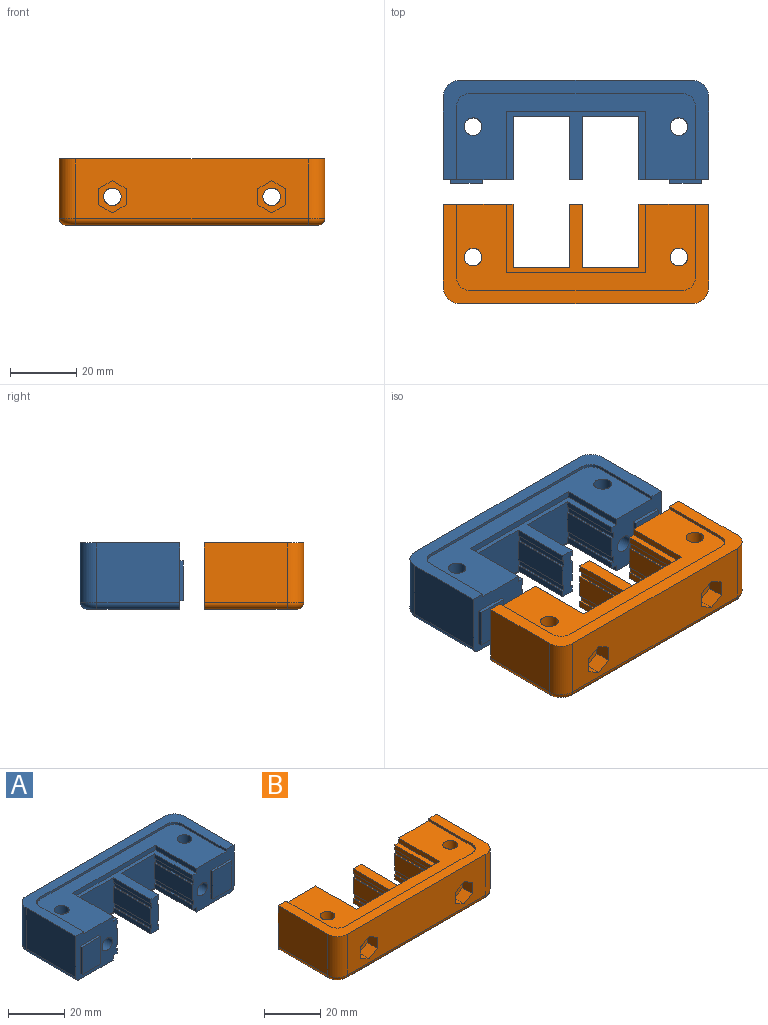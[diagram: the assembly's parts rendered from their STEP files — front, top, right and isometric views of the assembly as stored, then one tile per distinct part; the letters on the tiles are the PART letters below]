
ASSEMBLY  parts=2 mates=2
PART A: 89 faces, bbox 80.8x31.4x19.9 mm
  f0: plane 10.4x10.4mm, normal (0,0,-1), area 62.9mm2, adj f3,f9
  f1: plane 10.4x10.4mm, normal (0,0,-1), area 62.9mm2, adj f4,f10
  f2: cylinder r=2mm len=70mm, axis (1,0,0), area 219.9mm2, adj f5,f15,f16,f39
  f3: cylinder r=5.2mm len=10.4mm, axis (0,0,-1), area 163.4mm2, adj f0,f39
  f4: cylinder r=5.2mm len=10.4mm, axis (0,0,-1), area 163.4mm2, adj f1,f39
  f5: plane 70x17.9mm, normal (0,1,0), area 1083.1mm2, adj f2,f6,f7,f38,f70,f73
  f6: cylinder r=5mm len=17.9mm, axis (0,0,-1), area 140.6mm2, adj f5,f15,f37,f38
  f7: cylinder r=5mm len=17.9mm, axis (0,0,-1), area 140.6mm2, adj f5,f16,f35,f38
  f8: plane 64x0.9mm, normal (0,-1,0), area 57.6mm2, adj f11,f12,f33,f38
  f9: cylinder r=2.65mm len=14mm, axis (0,0,-1), area 233.1mm2, adj f0,f33
  f10: cylinder r=2.65mm len=14mm, axis (0,0,-1), area 233.1mm2, adj f1,f33
  f11: cylinder r=4mm len=4mm, axis (0,0,1), area 5.7mm2, adj f8,f32,f33,f38
  f12: cylinder r=4mm len=4mm, axis (0,0,1), area 5.7mm2, adj f8,f28,f33,f38
  f13: plane 41.9x2mm, normal (0,-1,0), area 83.8mm2, adj f25,f26,f27,f39
  f14: plane 41.9x2mm, normal (0,-1,0), area 83.8mm2, adj f29,f30,f31,f33
  f15: torus R=3mm, axis (0,0,-1), area 21.1mm2, adj f2,f6,f36,f39
  f16: torus R=3mm, axis (0,0,-1), area 21.1mm2, adj f2,f7,f34,f39
  f17: plane 18x15mm, normal (0,-1,0), area 258.4mm2, adj f25,f31,f40,f41,f42,f43,f44,f45
  f18: plane 18x15mm, normal (0,-1,0), area 258.4mm2, adj f19,f20,f21,f22,f23,f24,f25,f31
  f19: plane 19x2mm, normal (-1,0,0), area 38mm2, adj f18,f20,f21,f76
  f20: plane 19x0.53mm, normal (0,0,1), area 10mm2, adj f18,f19,f69,f76
  f21: plane 19x0.53mm, normal (0,0,-1), area 10mm2, adj f18,f19,f49,f76
  f22: plane 19x0.53mm, normal (0,0,-1), area 10mm2, adj f18,f24,f48,f77
  f23: plane 19x0.53mm, normal (0,0,1), area 10mm2, adj f18,f24,f64,f77
  f24: plane 19x2mm, normal (1,0,0), area 38mm2, adj f18,f22,f23,f77
  f25: plane 41.9x20.5mm, normal (0,0,-1), area 214.8mm2, adj f13,f17,f18,f26,f27,f54,f59,f63
  f26: plane 20.5x2mm, normal (1,0,0), area 41mm2, adj f13,f25,f39,f78
  f27: plane 20.5x2mm, normal (-1,0,0), area 41mm2, adj f13,f25,f39,f76
  f28: plane 22x0.9mm, normal (-1,0,0), area 19.8mm2, adj f12,f33,f38,f76
  f29: plane 20.5x2mm, normal (-1,0,0), area 41mm2, adj f14,f31,f33,f76
  f30: plane 20.5x2mm, normal (1,0,0), area 41mm2, adj f14,f31,f33,f78
  f31: plane 41.9x20.5mm, normal (0,0,1), area 214.9mm2, adj f14,f17,f18,f29,f30,f43,f47,f48
  f32: plane 22x0.9mm, normal (1,0,0), area 19.8mm2, adj f11,f33,f38,f78
  f33: plane 72x26mm, normal (0,0,1), area 962.1mm2, adj f8,f9,f10,f11,f12,f14,f28,f29
  f34: cylinder r=2mm len=25mm, axis (0,1,0), area 78.5mm2, adj f16,f35,f39,f78
  f35: plane 25x17.9mm, normal (-1,0,0), area 447.5mm2, adj f7,f34,f38,f78
  f36: cylinder r=2mm len=25mm, axis (0,-1,0), area 78.5mm2, adj f15,f37,f39,f76
  f37: plane 25x17.9mm, normal (1,0,0), area 447.5mm2, adj f6,f36,f38,f76
  f38: plane 80x30mm, normal (0,0,1), area 524.1mm2, adj f5,f6,f7,f8,f11,f12,f28,f32
  f39: plane 76x28mm, normal (0,0,-1), area 1095.3mm2, adj f2,f3,f4,f13,f15,f16,f26,f27
  f40: plane 19x0.53mm, normal (0,0,-1), area 10mm2, adj f17,f42,f43,f77
  f41: plane 19x0.53mm, normal (0,0,1), area 10mm2, adj f17,f42,f53,f77
  f42: plane 19x2mm, normal (-1,0,0), area 38mm2, adj f17,f40,f41,f77
  f43: plane 19x2mm, normal (-1,0,0), area 38mm2, adj f17,f31,f40,f77
  f44: plane 19x2mm, normal (1,0,0), area 38mm2, adj f17,f45,f46,f78
  f45: plane 19x0.53mm, normal (0,0,1), area 10mm2, adj f17,f44,f58,f78
  f46: plane 19x0.53mm, normal (0,0,-1), area 10mm2, adj f17,f44,f47,f78
  f47: plane 19x2mm, normal (1,0,0), area 38mm2, adj f17,f31,f46,f78
  f48: plane 19x2mm, normal (1,0,0), area 38mm2, adj f18,f22,f31,f77
  f49: plane 19x2mm, normal (-1,0,0), area 38mm2, adj f18,f21,f31,f76
  f50: plane 19x0.53mm, normal (0,0,-1), area 10mm2, adj f17,f52,f53,f77
  f51: plane 19x0.53mm, normal (0,0,1), area 10mm2, adj f17,f52,f54,f77
  f52: plane 19x2mm, normal (-1,0,0), area 38mm2, adj f17,f50,f51,f77
  f53: plane 19x7mm, normal (-1,0,0), area 133mm2, adj f17,f41,f50,f77
  f54: plane 19x2mm, normal (-1,0,0), area 38mm2, adj f17,f25,f51,f77
  f55: plane 19x2mm, normal (1,0,0), area 38mm2, adj f17,f56,f57,f78
  f56: plane 19x0.53mm, normal (0,0,1), area 10mm2, adj f17,f55,f59,f78
  f57: plane 19x0.53mm, normal (0,0,-1), area 10mm2, adj f17,f55,f58,f78
  f58: plane 19x7mm, normal (1,0,0), area 133mm2, adj f17,f45,f57,f78
  f59: plane 19x2mm, normal (1,0,0), area 38mm2, adj f17,f25,f56,f78
  f60: plane 19x0.53mm, normal (0,0,-1), area 10mm2, adj f18,f62,f64,f77
  f61: plane 19x0.53mm, normal (0,0,1), area 10mm2, adj f18,f62,f63,f77
  f62: plane 19x2mm, normal (1,0,0), area 38mm2, adj f18,f60,f61,f77
  f63: plane 19x2mm, normal (1,0,0), area 38mm2, adj f18,f25,f61,f77
  f64: plane 19x7mm, normal (1,0,0), area 133mm2, adj f18,f23,f60,f77
  f65: plane 19x2mm, normal (-1,0,0), area 38mm2, adj f18,f66,f67,f76
  f66: plane 19x0.53mm, normal (0,0,1), area 10mm2, adj f18,f65,f68,f76
  f67: plane 19x0.53mm, normal (0,0,-1), area 10mm2, adj f18,f65,f69,f76
  f68: plane 19x2mm, normal (-1,0,0), area 38mm2, adj f18,f25,f66,f76
  f69: plane 19x7mm, normal (-1,0,0), area 133mm2, adj f18,f20,f67,f76
  f70: cylinder r=5.2mm len=10.4mm, axis (0,1,0), area 163.4mm2, adj f5,f71
  f71: plane 10.4x10.4mm, normal (0,1,0), area 62.9mm2, adj f70,f72
  f72: cylinder r=2.65mm len=25mm, axis (0,1,0), area 416.3mm2, adj f71,f78
  f73: cylinder r=5.2mm len=10.4mm, axis (0,1,0), area 163.4mm2, adj f5,f74
  f74: plane 10.4x10.4mm, normal (0,1,0), area 62.9mm2, adj f73,f75
  f75: cylinder r=2.65mm len=25mm, axis (0,1,0), area 416.3mm2, adj f74,f76
  f76: plane 21.05x19.9mm, normal (0,-1,0), area 256.5mm2, adj f19,f20,f21,f25,f27,f28,f29,f31
  f77: plane 15x4mm, normal (0,-1,0), area 55.8mm2, adj f22,f23,f24,f25,f31,f40,f41,f42
  f78: plane 21.05x19.9mm, normal (0,-1,0), area 256.5mm2, adj f25,f26,f30,f31,f32,f33,f34,f35
  f79: plane 9.5x1mm, normal (0,0,-1), area 9.5mm2, adj f76,f80,f82,f83
  f80: plane 12x1mm, normal (1,0,0), area 12mm2, adj f76,f79,f81,f83
  f81: plane 9.5x1mm, normal (0,0,1), area 9.5mm2, adj f76,f80,f82,f83
  f82: plane 12x1mm, normal (-1,0,0), area 12mm2, adj f76,f79,f81,f83
  f83: plane 12x9.5mm, normal (0,-1,0), area 114mm2, adj f79,f80,f81,f82
  f84: plane 9.5x1mm, normal (0,0,1), area 9.5mm2, adj f78,f85,f87,f88
  f85: plane 12x1mm, normal (-1,0,0), area 12mm2, adj f78,f84,f86,f88
  f86: plane 9.5x1mm, normal (0,0,-1), area 9.5mm2, adj f78,f85,f87,f88
  f87: plane 12x1mm, normal (1,0,0), area 12mm2, adj f78,f84,f86,f88
  f88: plane 12x9.5mm, normal (0,-1,0), area 114mm2, adj f84,f85,f86,f87
PART B: 99 faces, bbox 80.8x30.4x19.9 mm
  f0: plane 21.05x19.9mm, normal (0,1,0), area 247.8mm2, adj f2,f3,f10,f16,f17,f20,f22,f45
  f1: plane 21.05x19.9mm, normal (0,1,0), area 247.8mm2, adj f6,f7,f12,f16,f17,f21,f26,f45
  f2: plane 19x7mm, normal (-1,0,0), area 133mm2, adj f0,f15,f82,f86
  f3: plane 19x2mm, normal (-1,0,0), area 38mm2, adj f0,f15,f54,f83
  f4: plane 19x7mm, normal (1,0,0), area 133mm2, adj f15,f78,f80,f88
  f5: plane 19x2mm, normal (1,0,0), area 38mm2, adj f15,f54,f77,f88
  f6: plane 19x2mm, normal (1,0,0), area 38mm2, adj f1,f14,f54,f74
  f7: plane 19x7mm, normal (1,0,0), area 133mm2, adj f1,f14,f71,f73
  f8: plane 19x2mm, normal (-1,0,0), area 38mm2, adj f14,f54,f68,f88
  f9: plane 19x7mm, normal (-1,0,0), area 133mm2, adj f14,f65,f69,f88
  f10: plane 19x2mm, normal (-1,0,0), area 38mm2, adj f0,f15,f55,f85
  f11: plane 19x2mm, normal (1,0,0), area 38mm2, adj f15,f55,f81,f88
  f12: plane 19x2mm, normal (1,0,0), area 38mm2, adj f1,f14,f55,f70
  f13: plane 19x2mm, normal (-1,0,0), area 38mm2, adj f14,f55,f66,f88
  f14: plane 18x15mm, normal (0,1,0), area 258.4mm2, adj f6,f7,f8,f9,f12,f13,f54,f55
  f15: plane 18x15mm, normal (0,1,0), area 258.4mm2, adj f2,f3,f4,f5,f10,f11,f54,f55
  f16: plane 76x28mm, normal (0,0,-1), area 1095.3mm2, adj f0,f1,f28,f30,f51,f52,f53,f59
  f17: plane 80x30mm, normal (0,0,1), area 524.1mm2, adj f0,f1,f22,f23,f24,f25,f26,f46
  f18: cylinder r=2.65mm len=14mm, axis (0,0,-1), area 233.1mm2, adj f27,f45
  f19: cylinder r=2.65mm len=14mm, axis (0,0,-1), area 233.1mm2, adj f29,f45
  f20: cylinder r=2.65mm len=25mm, axis (0,1,0), area 416.3mm2, adj f0,f44
  f21: cylinder r=2.65mm len=25mm, axis (0,1,0), area 416.3mm2, adj f1,f37
  f22: plane 25x17.9mm, normal (1,0,0), area 447.5mm2, adj f0,f17,f23,f59
  f23: cylinder r=5mm len=17.9mm, axis (0,0,-1), area 140.6mm2, adj f17,f22,f24,f60
  f24: plane 70x17.9mm, normal (0,-1,0), area 1130.8mm2, adj f17,f23,f25,f31,f32,f33,f34,f35
  f25: cylinder r=5mm len=17.9mm, axis (0,0,-1), area 140.6mm2, adj f17,f24,f26,f62
  f26: plane 25x17.9mm, normal (-1,0,0), area 447.5mm2, adj f1,f17,f25,f63
  f27: plane 10.4x10.4mm, normal (0,0,-1), area 62.9mm2, adj f18,f28
  f28: cylinder r=5.2mm len=10.4mm, axis (0,0,-1), area 163.4mm2, adj f16,f27
  f29: plane 10.4x10.4mm, normal (0,0,-1), area 62.9mm2, adj f19,f30
  f30: cylinder r=5.2mm len=10.4mm, axis (0,0,-1), area 163.4mm2, adj f16,f29
  f31: plane 5x4.2mm, normal (0.5,0,-0.87), area 24.2mm2, adj f24,f32,f36,f37
  f32: plane 5x4.85mm, normal (1,0,0), area 24.2mm2, adj f24,f31,f33,f37
  f33: plane 5x4.2mm, normal (0.5,0,0.87), area 24.2mm2, adj f24,f32,f34,f37
  f34: plane 5x4.2mm, normal (-0.5,0,0.87), area 24.2mm2, adj f24,f33,f35,f37
  f35: plane 5x4.85mm, normal (-1,0,0), area 24.2mm2, adj f24,f34,f36,f37
  f36: plane 5x4.2mm, normal (-0.5,0,-0.87), area 24.2mm2, adj f24,f31,f35,f37
  f37: plane 9.7x8.4mm, normal (0,-1,0), area 39mm2, adj f21,f31,f32,f33,f34,f35,f36
  f38: plane 5x4.2mm, normal (0.5,0,-0.87), area 24.2mm2, adj f24,f39,f43,f44
  f39: plane 5x4.85mm, normal (1,0,0), area 24.2mm2, adj f24,f38,f40,f44
  f40: plane 5x4.2mm, normal (0.5,0,0.87), area 24.2mm2, adj f24,f39,f41,f44
  f41: plane 5x4.2mm, normal (-0.5,0,0.87), area 24.2mm2, adj f24,f40,f42,f44
  f42: plane 5x4.85mm, normal (-1,0,0), area 24.2mm2, adj f24,f41,f43,f44
  f43: plane 5x4.2mm, normal (-0.5,0,-0.87), area 24.2mm2, adj f24,f38,f42,f44
  f44: plane 9.7x8.4mm, normal (0,-1,0), area 39mm2, adj f20,f38,f39,f40,f41,f42,f43
  f45: plane 72x26mm, normal (0,0,1), area 962.1mm2, adj f0,f1,f18,f19,f46,f47,f48,f49
  f46: plane 22x0.9mm, normal (1,0,0), area 19.8mm2, adj f1,f17,f45,f47
  f47: cylinder r=4mm len=4mm, axis (0,0,1), area 5.7mm2, adj f17,f45,f46,f48
  f48: plane 64x0.9mm, normal (0,1,0), area 57.6mm2, adj f17,f45,f47,f49
  f49: cylinder r=4mm len=4mm, axis (0,0,1), area 5.7mm2, adj f17,f45,f48,f50
  f50: plane 22x0.9mm, normal (-1,0,0), area 19.8mm2, adj f0,f17,f45,f49
  f51: plane 20.5x2mm, normal (-1,0,0), area 41mm2, adj f0,f16,f52,f54
  f52: plane 41.9x2mm, normal (0,1,0), area 83.8mm2, adj f16,f51,f53,f54
  f53: plane 20.5x2mm, normal (1,0,0), area 41mm2, adj f1,f16,f52,f54
  f54: plane 41.9x20.5mm, normal (0,0,-1), area 214.8mm2, adj f0,f1,f3,f5,f6,f8,f14,f15
  f55: plane 41.9x20.5mm, normal (0,0,1), area 214.8mm2, adj f0,f1,f10,f11,f12,f13,f14,f15
  f56: plane 20.5x2mm, normal (1,0,0), area 41mm2, adj f1,f45,f55,f57
  f57: plane 41.9x2mm, normal (0,1,0), area 83.8mm2, adj f45,f55,f56,f58
  f58: plane 20.5x2mm, normal (-1,0,0), area 41mm2, adj f0,f45,f55,f57
  f59: cylinder r=2mm len=25mm, axis (0,-1,0), area 78.5mm2, adj f0,f16,f22,f60
  f60: torus R=3mm, axis (0,0,-1), area 21.1mm2, adj f16,f23,f59,f61
  f61: cylinder r=2mm len=70mm, axis (-1,0,0), area 219.9mm2, adj f16,f24,f60,f62
  f62: torus R=3mm, axis (0,0,-1), area 21.1mm2, adj f16,f25,f61,f63
  f63: cylinder r=2mm len=25mm, axis (0,1,0), area 78.5mm2, adj f1,f16,f26,f62
  f64: plane 19x2mm, normal (-1,0,0), area 38mm2, adj f14,f65,f66,f88
  f65: plane 19x0.53mm, normal (0,0,1), area 10mm2, adj f9,f14,f64,f88
  f66: plane 19x0.53mm, normal (0,0,-1), area 10mm2, adj f13,f14,f64,f88
  f67: plane 19x2mm, normal (-1,0,0), area 38mm2, adj f14,f68,f69,f88
  f68: plane 19x0.53mm, normal (0,0,1), area 10mm2, adj f8,f14,f67,f88
  f69: plane 19x0.53mm, normal (0,0,-1), area 10mm2, adj f9,f14,f67,f88
  f70: plane 19x0.53mm, normal (0,0,-1), area 10mm2, adj f1,f12,f14,f72
  f71: plane 19x0.53mm, normal (0,0,1), area 10mm2, adj f1,f7,f14,f72
  f72: plane 19x2mm, normal (1,0,0), area 38mm2, adj f1,f14,f70,f71
  f73: plane 19x0.53mm, normal (0,0,-1), area 10mm2, adj f1,f7,f14,f75
  f74: plane 19x0.53mm, normal (0,0,1), area 10mm2, adj f1,f6,f14,f75
  f75: plane 19x2mm, normal (1,0,0), area 38mm2, adj f1,f14,f73,f74
  f76: plane 19x2mm, normal (1,0,0), area 38mm2, adj f15,f77,f78,f88
  f77: plane 19x0.53mm, normal (0,0,1), area 10mm2, adj f5,f15,f76,f88
  f78: plane 19x0.53mm, normal (0,0,-1), area 10mm2, adj f4,f15,f76,f88
  f79: plane 19x2mm, normal (1,0,0), area 38mm2, adj f15,f80,f81,f88
  f80: plane 19x0.53mm, normal (0,0,1), area 10mm2, adj f4,f15,f79,f88
  f81: plane 19x0.53mm, normal (0,0,-1), area 10mm2, adj f11,f15,f79,f88
  f82: plane 19x0.53mm, normal (0,0,-1), area 10mm2, adj f0,f2,f15,f84
  f83: plane 19x0.53mm, normal (0,0,1), area 10mm2, adj f0,f3,f15,f84
  f84: plane 19x2mm, normal (-1,0,0), area 38mm2, adj f0,f15,f82,f83
  f85: plane 19x0.53mm, normal (0,0,-1), area 10mm2, adj f0,f10,f15,f87
  f86: plane 19x0.53mm, normal (0,0,1), area 10mm2, adj f0,f2,f15,f87
  f87: plane 19x2mm, normal (-1,0,0), area 38mm2, adj f0,f15,f85,f86
  f88: plane 15x4mm, normal (0,1,0), area 55.8mm2, adj f4,f5,f8,f9,f11,f13,f54,f55
  f89: plane 12.4x1.3mm, normal (1,0,0), area 16.1mm2, adj f1,f90,f92,f93
  f90: plane 9.9x1.3mm, normal (0,0,-1), area 12.9mm2, adj f1,f89,f91,f93
  f91: plane 12.4x1.3mm, normal (-1,0,0), area 16.1mm2, adj f1,f90,f92,f93
  f92: plane 9.9x1.3mm, normal (0,0,1), area 12.9mm2, adj f1,f89,f91,f93
  f93: plane 12.4x9.9mm, normal (0,1,0), area 122.8mm2, adj f89,f90,f91,f92
  f94: plane 12.4x1.3mm, normal (-1,0,0), area 16.1mm2, adj f0,f95,f97,f98
  f95: plane 9.9x1.3mm, normal (0,0,1), area 12.9mm2, adj f0,f94,f96,f98
  f96: plane 12.4x1.3mm, normal (1,0,0), area 16.1mm2, adj f0,f95,f97,f98
  f97: plane 9.9x1.3mm, normal (0,0,-1), area 12.9mm2, adj f0,f94,f96,f98
  f98: plane 12.4x9.9mm, normal (0,1,0), area 122.8mm2, adj f94,f95,f96,f97
PLACE A t=(-25.09,-38.64,9.76)mm
PLACE B t=(-25.09,-45.95,9.76)mm
MATE planar A.f35 <-> B.f26  axis (-1,0,0) through (-65.09,-26.14,21.16)mm
MATE planar B.f45 <-> A.f33  axis (0,0,1) through (-46.04,-56.2,20.26)mm
